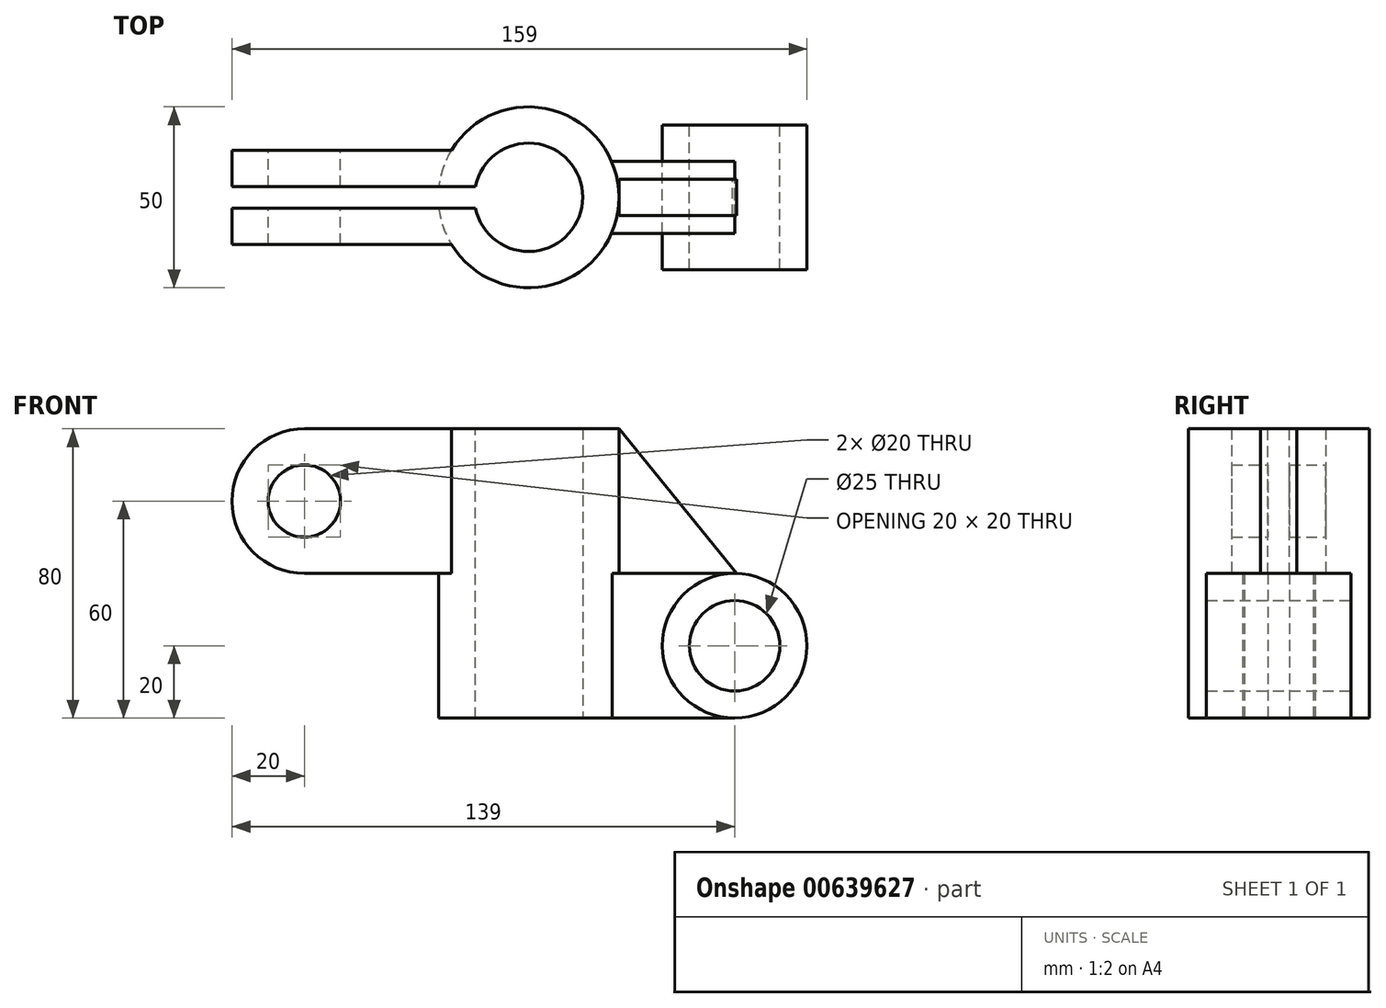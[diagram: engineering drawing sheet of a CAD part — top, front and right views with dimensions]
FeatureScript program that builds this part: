
annotation { "Feature Type Name" : "Feature", "Feature Type Description" : "" }
export const myFeature = defineFeature(function(context is Context, id is Id, definition is map)
    precondition{}
    {
        {
            var Q0;
            Q0=qCreatedBy(makeId("Top.planeOp"),FACE);
            var sketch = newSketch(context, id + "F0", { "sketchPlane" : qUnion([Q0])});
            skCircle(sketch, "E0", {"center": v(0, 0) * mm, "radius": 15 * mm});
            skCircle(sketch, "E1", {"center": v(0, 0) * mm, "radius": 25 * mm});
            skSolve(sketch);
        }
        {
            var Q0;
            Q0 = qSketchRegion(id + "F0", true);
            extrude(context, id + "F1", {"entities" : qUnion([Q0]), "depth" : 80 * mm, "offsetDistance" : 25 * mm});
        }
        {
            var Q0;
            Q0=qCreatedBy(makeId("Front.planeOp"),FACE);
            var sketch = newSketch(context, id + "F2", { "sketchPlane" : qUnion([Q0])});
            skLineSegment(sketch, "E2", {"start": v(-25, 0) * mm, "end": v(-25, 80) * mm});
            skLineSegment(sketch, "E3", {"start": v(25, 80) * mm, "end": v(25, 0) * mm});
            skLineSegment(sketch, "E4", {"start": v(-25, 80) * mm, "end": v(-62, 80) * mm});
            skLineSegment(sketch, "E5", {"start": v(-62, 80) * mm, "end": v(-62, 40) * mm});
            skLineSegment(sketch, "E6", {"start": v(-62, 40) * mm, "end": v(-25, 40) * mm});
            skCircle(sketch, "E7", {"center": v(-62, 60) * mm, "radius": 10 * mm});
            skPoint(sketch, "E7.centerSnap0", {"position": v(-62, 60) * mm});
            skCircle(sketch, "E8", {"center": v(-62, 60) * mm, "radius": 20 * mm});
            skSolve(sketch);
        }
        {
            var Q0;
            Q0 = qSketchRegion(id + "F2", true);
            extrude(context, id + "F3", {"entities" : qUnion([Q0]), "depth" : 13 * mm, "offsetDistance" : 25 * mm, "hasSecondDirection" : true, "secondDirectionOppositeDirection" : true, "secondDirectionDepth" : 13 * mm});
        }
        {
            var Q0;
            Q0=makeQuery(id+"F3.opExtrude","SWEPT_FACE",FACE,{"disambiguationData":[OSD([sQuery(id+"F2.wireOp",EDGE,"E2")])]});
            extrude(context, id + "F4", {"entities" : qUnion([Q0]), "operationType" : NewBodyOperationType.ADD, "depth" : 4.5 * mm, "offsetDistance" : 25 * mm});
        }
        {
            var Q0;
            {var subQ0=sQuery(id+"F2.wireOp",EDGE,"E4");Q0=makeQuery(id+"F4.boolean.opBoolean","MERGE",FACE,{"derivedFrom":[makeQuery(id+"F1.opExtrude","CAP_FACE",FACE,{"disambiguationData":[OSD([sQuery(id+"F0.wireOp",EDGE,"E0"),sQuery(id+"F0.wireOp",EDGE,"E1")])],"isStart":false}),makeQuery(id+"F3.opExtrude","SWEPT_FACE",FACE,{"disambiguationData":[OSD([subQ0])]}),makeQuery(id+"F4.opExtrude","SWEPT_FACE",FACE,{"disambiguationData":[OSD([sQuery(id+"F2.wireOp",EDGE,"E2"),subQ0])]})]});}
            var sketch = newSketch(context, id + "F5", { "sketchPlane" : qUnion([Q0])});
            skLineSegment(sketch, "E9", {"start": v(-15, 0) * mm, "end": v(-90.18, 0) * mm});
            skPoint(sketch, "E9.endSnap0", {"position": v(-62, 0) * mm});
            skLineSegment(sketch, "E10", {"start": v(-15, 0) * mm, "end": v(-14.7, 2.98) * mm});
            skLineSegment(sketch, "E11", {"start": v(-14.7, 2.98) * mm, "end": v(-90.18, 3) * mm});
            skLineSegment(sketch, "E12", {"start": v(-14.7, -3) * mm, "end": v(-91.14, -3) * mm});
            skLineSegment(sketch, "E13", {"start": v(-90.18, 3) * mm, "end": v(-90.18, -3) * mm});
            skLineSegment(sketch, "E14", {"start": v(-90.18, -3) * mm, "end": v(-90.18, -13) * mm});
            skLineSegment(sketch, "E15", {"start": v(-90.18, -13) * mm, "end": v(-7.48, -13) * mm});
            skLineSegment(sketch, "E16", {"start": v(-90.18, 3) * mm, "end": v(-90.18, 13) * mm});
            skLineSegment(sketch, "E17", {"start": v(-90.18, 13) * mm, "end": v(-7.48, 13) * mm});
            skSolve(sketch);
        }
        {
            var Q0;
            {var subQ0=sQuery(id+"F5.wireOp",EDGE,"E13");var subQ1=sQuery(id+"F5.wireOp",EDGE,"E9");var subQ2=makeQuery(id+"F5.imprint","INTERSECT",VERTEX,{"derivedFrom":[subQ1,subQ0]});Q0=makeQuery(id+"F5.imprint","IMPRINT",FACE,{"disambiguationData":[TD([[makeQuery(id+"F5.imprint","IMPRINT",EDGE,{"disambiguationData":[TD([[subQ2,1.0]])],"derivedFrom":subQ0}),1.0]])]});}
            var Q1;
            {var subQ0=sQuery(id+"F5.wireOp",EDGE,"E13");var subQ1=sQuery(id+"F5.wireOp",EDGE,"E9");var subQ2=makeQuery(id+"F5.imprint","INTERSECT",VERTEX,{"derivedFrom":[subQ1,subQ0]});Q1=makeQuery(id+"F5.imprint","IMPRINT",FACE,{"disambiguationData":[TD([[makeQuery(id+"F5.imprint","IMPRINT",EDGE,{"disambiguationData":[TD([[subQ2,-1.0]])],"derivedFrom":subQ0}),1.0]])]});}
            var Q2;
            {var subQ0=sQuery(id+"F5.wireOp",EDGE,"E10");var subQ1=sQuery(id+"F5.wireOp",EDGE,"E9");var subQ2=makeQuery(id+"F1.opExtrude","CAP_EDGE",EDGE,{"disambiguationData":[OSD([sQuery(id+"F0.wireOp",EDGE,"E0")])],"isStart":false});var subQ3=makeQuery(id+"F5.imprint","INTERSECT",VERTEX,{"derivedFrom":[subQ2,subQ1,subQ0]});Q2=makeQuery(id+"F5.imprint","IMPRINT",FACE,{"disambiguationData":[TD([[makeQuery(id+"F5.imprint","IMPRINT",EDGE,{"disambiguationData":[TD([[subQ3,1.0]])],"derivedFrom":subQ2}),-1.0]])]});}
            var Q3;
            {var subQ1=makeQuery(id+"F1.opExtrude","CAP_EDGE",EDGE,{"disambiguationData":[OSD([sQuery(id+"F0.wireOp",EDGE,"E0")])],"isStart":false});var subQ5=sQuery(id+"F5.wireOp",EDGE,"E12");var subQ6=makeQuery(id+"F5.imprint","INTERSECT",VERTEX,{"derivedFrom":[subQ1,subQ5]});Q3=makeQuery(id+"F5.imprint","IMPRINT",FACE,{"disambiguationData":[TD([[makeQuery(id+"F5.imprint","IMPRINT",EDGE,{"disambiguationData":[TD([[subQ6,1.0]])],"derivedFrom":subQ1}),-1.0]])]});}
            extrude(context, id + "F6", {"entities" : qUnion([Q0, Q1, Q2, Q3]), "operationType" : NewBodyOperationType.REMOVE, "oppositeDirection" : true, "depth" : 99.3 * mm, "offsetDistance" : 25 * mm});
        }
        {
            var Q0;
            Q0=qCreatedBy(makeId("Front.planeOp"),FACE);
            var sketch = newSketch(context, id + "F7", { "sketchPlane" : qUnion([Q0])});
            skLineSegment(sketch, "E18", {"start": v(25, 80) * mm, "end": v(25, 0) * mm});
            skLineSegment(sketch, "E19", {"start": v(25, 0) * mm, "end": v(57, 0) * mm});
            skLineSegment(sketch, "E20", {"start": v(57, 0) * mm, "end": v(57, 40) * mm});
            skLineSegment(sketch, "E21", {"start": v(57, 40) * mm, "end": v(25, 40) * mm});
            skCircle(sketch, "E22", {"center": v(57, 20) * mm, "radius": 20 * mm});
            skPoint(sketch, "E22.centerSnap0", {"position": v(57, 20) * mm});
            skCircle(sketch, "E23", {"center": v(57, 20) * mm, "radius": 12.5 * mm});
            skSolve(sketch);
        }
        {
            var Q0;
            {var subQ0=sQuery(id+"F7.wireOp",EDGE,"E19");Q0=makeQuery(id+"F7.imprint","IMPRINT",FACE,{"disambiguationData":[TD([[makeQuery(id+"F7.imprint","IMPRINT",EDGE,{"derivedFrom":subQ0}),1.0]])]});}
            extrude(context, id + "F8", {"entities" : qUnion([Q0]), "depth" : 10 * mm, "offsetDistance" : 25 * mm, "hasSecondDirection" : true, "secondDirectionOppositeDirection" : true, "secondDirectionDepth" : 10 * mm});
        }
        {
            var Q0;
            {var subQ1=sQuery(id+"F7.wireOp",EDGE,"E20");var subQ3=sQuery(id+"F7.wireOp",EDGE,"E23");var subQ4=makeQuery(id+"F7.imprint","INTERSECT",VERTEX,{"disambiguationData":[OD(0.0)],"derivedFrom":[subQ1,subQ3]});Q0=makeQuery(id+"F7.imprint","IMPRINT",FACE,{"disambiguationData":[TD([[makeQuery(id+"F7.imprint","IMPRINT",EDGE,{"disambiguationData":[TD([[subQ4,-1.0]])],"derivedFrom":subQ3}),-1.0]])]});}
            var Q1;
            {var subQ1=sQuery(id+"F7.wireOp",EDGE,"E20");var subQ3=sQuery(id+"F7.wireOp",EDGE,"E23");var subQ4=makeQuery(id+"F7.imprint","INTERSECT",VERTEX,{"disambiguationData":[OD(0.0)],"derivedFrom":[subQ1,subQ3]});Q1=makeQuery(id+"F7.imprint","IMPRINT",FACE,{"disambiguationData":[TD([[makeQuery(id+"F7.imprint","IMPRINT",EDGE,{"disambiguationData":[TD([[subQ4,1.0]])],"derivedFrom":subQ3}),-1.0]])]});}
            extrude(context, id + "F9", {"entities" : qUnion([Q0, Q1]), "depth" : 20 * mm, "offsetDistance" : 25 * mm, "hasSecondDirection" : true, "secondDirectionOppositeDirection" : true, "secondDirectionDepth" : 20 * mm});
        }
        {
            var Q0;
            Q0=makeQuery(id+"F8.opExtrude","SWEPT_FACE",FACE,{"disambiguationData":[OSD([sQuery(id+"F7.wireOp",EDGE,"E18")])]});
            extrude(context, id + "F10", {"entities" : qUnion([Q0]), "operationType" : NewBodyOperationType.ADD, "depth" : 1.9 * mm, "offsetDistance" : 25 * mm});
        }
        {
            var Q0;
            Q0=qCreatedBy(makeId("Front.planeOp"),FACE);
            var sketch = newSketch(context, id + "F11", { "sketchPlane" : qUnion([Q0])});
            skLineSegment(sketch, "E24", {"start": v(25, 80) * mm, "end": v(25, 40) * mm});
            skCircle(sketch, "E25.0.0", {"center": v(57, 20) * mm, "radius": 20 * mm});
            skLineSegment(sketch, "E26", {"start": v(25, 80) * mm, "end": v(57.6, 40) * mm});
            skLineSegment(sketch, "E27", {"start": v(25, 40) * mm, "end": v(57.6, 40) * mm});
            skSolve(sketch);
        }
        {
            var Q0;
            {var subQ1=sQuery(id+"F11.wireOp",EDGE,"E26");Q0=makeQuery(id+"F11.imprint","IMPRINT",FACE,{"disambiguationData":[TD([[makeQuery(id+"F11.imprint","IMPRINT",EDGE,{"derivedFrom":subQ1}),-1.0]])]});}
            extrude(context, id + "F12", {"entities" : qUnion([Q0]), "depth" : 5 * mm, "offsetDistance" : 25 * mm, "hasSecondDirection" : true, "secondDirectionOppositeDirection" : true, "secondDirectionDepth" : 5 * mm});
        }
    });
